# Revit family: Water_Softening_Systems-Commercial-Duplex_Alternating-WATTS-Locksmith-CLSTA_Series
name_source: partatom
category: Pipe Accessories
units: mm (PartAtom-declared; Revit-internal decimal feet)

## family parameters
Always vertical = No
Cut with Voids When Loaded = No
OmniClass Number = 23.65.50.11.11.14
OmniClass Title = Water Softeners
Part Type = Normal
Round Connector Dimension = Use Diameter
Shared = Yes
Work Plane-Based = Yes

## types (13) — shared parameters
Assembly Code = D2090600
Brine Tank Material = Plastic-Watts-Polyethylene-Black
Country = United States
Default Elevation = 0"
Description = LOCKSMITH™ Series CLS Softeners for Hardness Reduction with Watts Exclusive Valve Controller, Pipe Size 1.5 - 2 IN
Drop PSI = 15/25
Electrical Requirement = 120V (60Hz)
Flow Rate = up to 119 gpm
Free Chlorine = 1mg/L
Hardness (Maximum) = Depends on customers acceptable hardness leakage level.
IAPMO Compliance = Control Valve - Certified to NSF/ANSI Std. 61 and 372; Ion Exchange Resin - Certified to NSF/ANSI Std. 61 and 372; Mineral Tank - Certified to NSF/ANSI Std. 44 or 61
Installation Instruction Link = https://www.watts.com
Iron = 1mg/L
Manufacturer = WATTS
Manufacturer Product Line = Backwashing Systems
Material = Plastic-Watts-Fibreglass
Mineral Tank Material = Plastic-Watts-Fibreglass
Oil and H2S = None Allowed
Price = Prices may vary. Please consult Manufacturer Representative for most up-to-date price list.
Product Documentation Link = https://www.watts.com
Product Page URL = https://www.watts.com
Region = North America
Temperature Range = 34 - 110°F (1 - 43°C)
Total Dissolved Solids = Must be below 750 mg/l for the softener to produce less than 1 grain per gallon soft water
Turbidity = Less than 5.0 NTU
URL = https://www.watts.com
Valve Material = Metal-Watts-Brass
Water Pressure = 25 psi to 125 psi (171 kPa to 8.5 bar
distance = 5/16"
pH = 6 to 10

## per-type parameters (varying)
- M4410LTA: A and B=53 1/4"; Backwash Flow Rate=4; Brine Tank Radius=9"; C=61"; Connection Radius=3/4"; Connection Size=1 1/2"; D=12"; E=52"; F=18"; FT3 Resin=3; G=40"; Gravel=30 lbs.; Inlet 2 Connection Description=1 1/2" Inlet 2 Supply Connection; Inlet Connection Description=1 1/2" Inlet Supply Connection; LBS. Salt Per Regeneration=12-30 lbs.; Masking Radius=6 1/4"; Mineral Tank Height=52"; Mineral Tank Radius=6"; Mineral Tank Size Width=12"; Order Code:=68110951; Outlet 2 Connection Description=1 1/2" Outlet 2 Supply Connection; Outlet Connection Description=1 1/2" Outlet Supply Connection; Salt Fill=400; Service Flow Rate=25 gpm/40 gpm; Shipping Weight=420 lbs. (190 kg.); Softening  (Min - Max)=40K-60K; Space Required (D X W X H)=24" x 64" x 75"; Type Comments=2 Cubic Foot 1 1/2" Duplex Alternating Softener with Flow Meter
- M4414LTA: A and B=68 1/4"; Backwash Flow Rate=5; Brine Tank Radius=9"; C=73 5/8"; Connection Radius=3/4"; Connection Size=1 1/2"; D=14"; E=60"; F=18"; FT3 Resin=3; G=40"; Gravel=60 lbs.; Inlet 2 Connection Description=1 1/2" Inlet 2 Supply Connection; Inlet Connection Description=1 1/2" Inlet Supply Connection; LBS. Salt Per Regeneration=18-45 lbs.; Masking Radius=7 1/4"; Mineral Tank Height=65"; Mineral Tank Radius=7"; Mineral Tank Size Width=14"; Order Code:=68110952; Outlet 2 Connection Description=1 1/2" Outlet 2 Supply Connection; Outlet Connection Description=1 1/2" Outlet Supply Connection; Salt Fill=400; Service Flow Rate=35 gpm/55 gpm; Shipping Weight=480 lbs. (218kg.); Softening  (Min - Max)=60K-90K; Space Required (D X W X H)=24" x 64" x 75"; Type Comments=3 Cubic Foot 1 1/2" Duplex Alternating Softener with Flow Meter
- M4418LTA: A and B=68 1/4"; Backwash Flow Rate=7; Brine Tank Radius=9"; C=73 5/8"; Connection Radius=3/4"; Connection Size=1 1/2"; D=16"; E=60"; F=18"; FT3 Resin=4; G=40"; Gravel=80 lbs.; Inlet 2 Connection Description=1 1/2" Inlet 2 Supply Connection; Inlet Connection Description=1 1/2" Inlet Supply Connection; LBS. Salt Per Regeneration=24-60 lbs.; Masking Radius=8 1/4"; Mineral Tank Height=65"; Mineral Tank Radius=8"; Mineral Tank Size Width=16"; Order Code:=68110955; Outlet 2 Connection Description=1 1/2" Outlet 2 Supply Connection; Outlet Connection Description=1 1/2" Outlet Supply Connection; Salt Fill=400; Service Flow Rate=57 gpm/65 gpm; Shipping Weight=640 lbs. (290 kg.); Softening  (Min - Max)=80K-120K; Space Required (D X W X H)=24" x 64" x 75"; Type Comments=4 Cubic Foot 1 1/2" Duplex Alternating Softener with Flow Meter
- M4422LTA: A and B=68 1/4"; Backwash Flow Rate=11; Brine Tank Radius=12"; C=73 5/8"; Connection Radius=3/4"; Connection Size=1 1/2"; D=18"; E=70"; F=24"; FT3 Resin=5; G=41"; Gravel=100 lbs.; Inlet 2 Connection Description=1 1/2" Inlet 2 Supply Connection; Inlet Connection Description=1 1/2" Inlet Supply Connection; LBS. Salt Per Regeneration=30-75 lbs.; Masking Radius=9 1/4"; Mineral Tank Height=65"; Mineral Tank Radius=9"; Mineral Tank Size Width=18"; Order Code:=68110957; Outlet 2 Connection Description=1 1/2" Outlet 2 Supply Connection; Outlet Connection Description=1 1/2" Outlet Supply Connection; Salt Fill=600; Service Flow Rate=60 gpm/ 77 gpm; Shipping Weight=760 lbs. (345 kg.); Softening  (Min - Max)=100K-150K; Space Required (D X W X H)=24" x 68" x 89"; Type Comments=5 Cubic Foot 1 1/2" Duplex Alternating Softener with Flow Meter
- M4426LTA: A and B=65 1/4"; Backwash Flow Rate=13; Brine Tank Radius=12"; C=70 5/8"; Connection Radius=3/4"; Connection Size=1 1/2"; D=21"; E=75"; F=24"; FT3 Resin=7; G=41"; Gravel=100 lbs.; Inlet 2 Connection Description=1 1/2" Inlet 2 Supply Connection; Inlet Connection Description=1 1/2" Inlet Supply Connection; LBS. Salt Per Regeneration=42-105 lbs.; Masking Radius=10 3/4"; Mineral Tank Height=62"; Mineral Tank Radius=10 1/2"; Mineral Tank Size Width=21"; Order Code:=68110962; Outlet 2 Connection Description=1 1/2" Outlet 2 Supply Connection; Outlet Connection Description=1 1/2" Outlet Supply Connection; Salt Fill=800; Service Flow Rate=74 gpm/ 97 gpm; Shipping Weight=1170 lbs. (531 kg.); Softening  (Min - Max)=140K-210K; Space Required (D X W X H)=24" x 72" x 84"; Type Comments=7 Cubic Foot 1 1/2" Duplex Alternating Softener with Flow Meter
- M4430LTA: A and B=75 1/4"; Backwash Flow Rate=15; Brine Tank Radius=15"; C=80 5/8"; Connection Radius=3/4"; Connection Size=1 1/2"; D=24"; E=87"; F=30"; FT3 Resin=10; G=50"; Gravel=200 lbs.; Inlet 2 Connection Description=1 1/2" Inlet 2 Supply Connection; Inlet Connection Description=1 1/2" Inlet Supply Connection; LBS. Salt Per Regeneration=60-150 lbs.; Masking Radius=12 1/4"; Mineral Tank Height=72"; Mineral Tank Radius=12"; Mineral Tank Size Width=24"; Order Code:=68110967; Outlet 2 Connection Description=1 1/2" Outlet 2 Supply Connection; Outlet Connection Description=1 1/2" Outlet Supply Connection; Salt Fill=1400; Service Flow Rate=80 gpm/ 100 gpm; Shipping Weight=1420 lbs. (644 kg.); Softening  (Min - Max)=200K-300K; Space Required (D X W X H)=30" x 89" x 96"; Type Comments=10 Cubic Foot 1 1/2" Duplex Alternating Softener with Flow Meter
- M4543LTA: A and B=68 1/2"; Backwash Flow Rate=5; Brine Tank Radius=9"; C=74 1/4"; Connection Radius=1"; Connection Size=2"; D=15"; E=52"; F=18"; FT3 Resin=3; G=40"; Gravel=60 lbs.; Inlet 2 Connection Description=2" Inlet 2 Supply Connection; Inlet Connection Description=2" Inlet Supply Connection; LBS. Salt Per Regeneration=18-45 lbs.; Masking Radius=7 1/4"; Mineral Tank Height=65"; Mineral Tank Radius=7"; Mineral Tank Size Width=14"; Order Code:=68110972; Outlet 2 Connection Description=2" Outlet 2 Supply Connection; Outlet Connection Description=2" Outlet Supply Connection; Salt Fill=400; Service Flow Rate=39 gpm/55 gpm; Shipping Weight=530 lbs. (240 kg.); Softening  (Min - Max)=60K-90K; Space Required (D X W X H)=24" x 64" x 87"; Type Comments=3 Cubic Foot 2" Duplex Alternating Softener with Flow Meter
- M4547LTA: A and B=68 1/2"; Backwash Flow Rate=7; Brine Tank Radius=9"; C=74 1/4"; Connection Radius=1"; Connection Size=2"; D=16"; E=60"; F=18"; FT3 Resin=4; G=40"; Gravel=80 lbs.; Inlet 2 Connection Description=2" Inlet 2 Supply Connection; Inlet Connection Description=2" Inlet Supply Connection; LBS. Salt Per Regeneration=24-60 lbs.; Masking Radius=8 1/4"; Mineral Tank Height=65"; Mineral Tank Radius=8"; Mineral Tank Size Width=16"; Order Code:=68110974; Outlet 2 Connection Description=2" Outlet 2 Supply Connection; Outlet Connection Description=2" Outlet Supply Connection; Salt Fill=400; Service Flow Rate=47 gpm/60 gpm; Shipping Weight=700 lbs. (318 kg.); Softening  (Min - Max)=80K-120K; Space Required (D X W X H)=24" x 64" x 87"; Type Comments=4 Cubic Foot 2" Duplex Alternating Softener with Flow Meter
- M4548LTA: A and B=68 1/2"; Backwash Flow Rate=10; Brine Tank Radius=12"; C=74 1/4"; Connection Radius=1"; Connection Size=2"; D=18"; E=60"; F=24"; FT3 Resin=5; G=41"; Gravel=100 lbs.; Inlet 2 Connection Description=2" Inlet 2 Supply Connection; Inlet Connection Description=2" Inlet Supply Connection; LBS. Salt Per Regeneration=30-75 lbs.; Masking Radius=9 1/4"; Mineral Tank Height=65"; Mineral Tank Radius=9"; Mineral Tank Size Width=18"; Order Code:=68110976; Outlet 2 Connection Description=2" Outlet 2 Supply Connection; Outlet Connection Description=2" Outlet Supply Connection; Salt Fill=600; Service Flow Rate=53 gpm/69 gpm; Shipping Weight=800 lbs. (362 kg.); Softening  (Min - Max)=100K-150K; Space Required (D X W X H)=24" x 68" x 89"; Type Comments=5 Cubic Foot 2" Duplex Alternating Softener with Flow Meter
- M4552LTA: A and B=65 1/2"; Backwash Flow Rate=13; Brine Tank Radius=12"; C=73"; Connection Radius=1"; Connection Size=2"; D=21"; E=70"; F=24"; FT3 Resin=7; G=41"; Gravel=100 lbs.; Inlet 2 Connection Description=2" Inlet 2 Supply Connection; Inlet Connection Description=2" Inlet Supply Connection; LBS. Salt Per Regeneration=42-105 lbs.; Masking Radius=10 3/4"; Mineral Tank Height=62"; Mineral Tank Radius=10 1/2"; Mineral Tank Size Width=21"; Order Code:=68110981; Outlet 2 Connection Description=2" Outlet 2 Supply Connection; Outlet Connection Description=2" Outlet Supply Connection; Salt Fill=600; Service Flow Rate=66 gpm/85 gpm; Shipping Weight=1200 lbs. (544 kg.); Softening  (Min - Max)=140K-210K; Space Required (D X W X H)=24" x 72" x 89"; Type Comments=7 Cubic Foot 2" Duplex Alternating Softener with Flow Meter
- M4558LTA: A and B=75 1/2"; Backwash Flow Rate=15; Brine Tank Radius=15"; C=83"; Connection Radius=1"; Connection Size=2"; D=24"; E=75"; F=30"; FT3 Resin=10; G=50"; Gravel=200 lbs.; Inlet 2 Connection Description=2" Inlet 2 Supply Connection; Inlet Connection Description=2" Inlet Supply Connection; LBS. Salt Per Regeneration=60-150 lbs.; Masking Radius=12 1/4"; Mineral Tank Height=72"; Mineral Tank Radius=12"; Mineral Tank Size Width=24"; Order Code:=68110986; Outlet 2 Connection Description=2" Outlet 2 Supply Connection; Outlet Connection Description=2" Outlet Supply Connection; Salt Fill=1400; Service Flow Rate=73gpm/94 gpm; Shipping Weight=1420 lbs. (644kg.); Softening  (Min - Max)=200K-300K; Space Required (D X W X H)=30" x 89" x 96"; Type Comments=10 Cubic Foot 2" Duplex Alternating Softener with Flow Meter
- M4559LTA: A and B=75 1/2"; Backwash Flow Rate=25; Brine Tank Radius=19 1/2"; C=83"; Connection Radius=1"; Connection Size=2"; D=30"; E=87"; F=39"; FT3 Resin=15; G=48"; Gravel=400 lbs.; Inlet 2 Connection Description=2" Inlet 2 Supply Connection; Inlet Connection Description=2" Inlet Supply Connection; LBS. Salt Per Regeneration=90-225 lbs.; Masking Radius=15 1/4"; Mineral Tank Height=72"; Mineral Tank Radius=15"; Mineral Tank Size Width=30"; Order Code:=68110992; Outlet 2 Connection Description=2" Outlet 2 Supply Connection; Outlet Connection Description=2" Outlet Supply Connection; Salt Fill=2200; Service Flow Rate=84gpm/109 gpm; Shipping Weight=2320 lbs. (1052kg.); Softening  (Min - Max)=300K-450K; Space Required (D X W X H)=39" x 95" x 106"; Type Comments=15 Cubic Foot 2" Duplex Alternating Softener with Flow Meter
- M4560LTA: A and B=75 1/2"; Backwash Flow Rate=35; Brine Tank Radius=19 1/2"; C=83"; Connection Radius=1"; Connection Size=2"; D=36"; E=93"; F=39"; FT3 Resin=20; G=48"; Gravel=500 lbs.; Inlet 2 Connection Description=2" Inlet 2 Supply Connection; Inlet Connection Description=2" Inlet Supply Connection; LBS. Salt Per Regeneration=120-300 lbs.; Masking Radius=18 1/4"; Mineral Tank Height=72"; Mineral Tank Radius=18"; Mineral Tank Size Width=36"; Order Code:=68110997; Outlet 2 Connection Description=2" Outlet 2 Supply Connection; Outlet Connection Description=2" Outlet Supply Connection; Salt Fill=2200; Service Flow Rate=93gpm/119 gpm; Shipping Weight=2840 lbs. (1414kg.); Softening  (Min - Max)=400K-600K; Space Required (D X W X H)=39" x 101" x 107"; Type Comments=20 Cubic Foot 2" Duplex Alternating Softener with Flow Meter

note: column(s) folded — value = type name in every type: Model

## geometry (parser evidence)
native form markers: Sweep x4
no freeform markers — native parametric forms only
